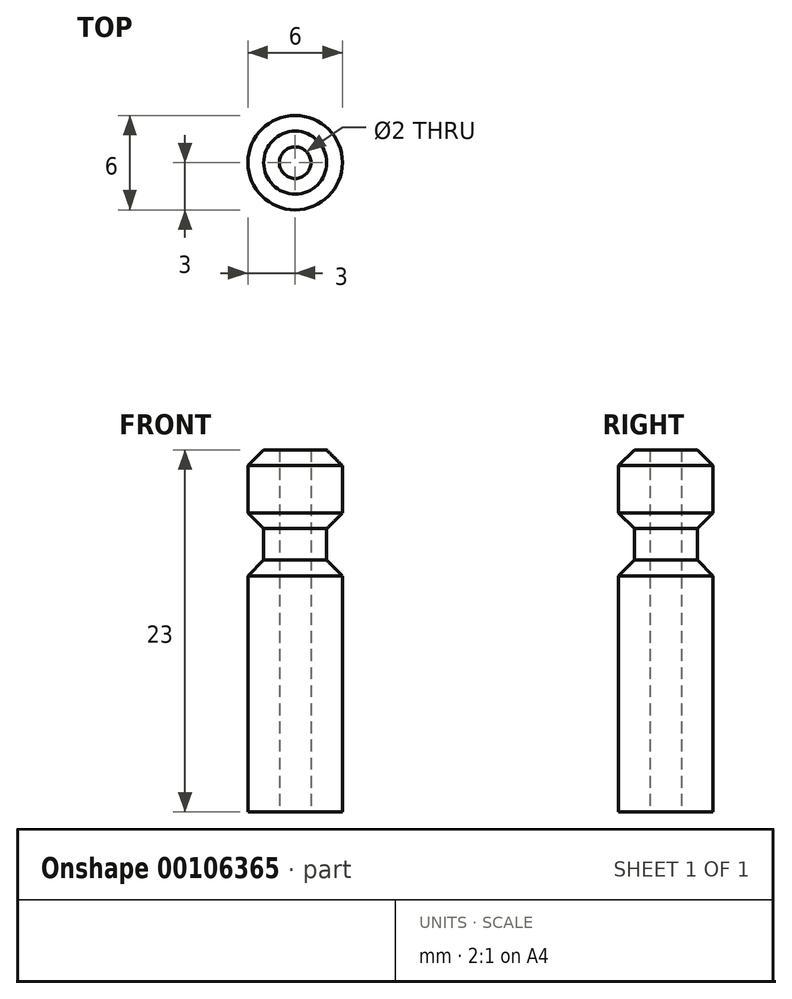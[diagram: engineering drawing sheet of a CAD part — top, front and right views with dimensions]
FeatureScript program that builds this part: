
annotation { "Feature Type Name" : "Feature", "Feature Type Description" : "" }
export const myFeature = defineFeature(function(context is Context, id is Id, definition is map)
    precondition{}
    {
        {
            var Q0;
            Q0=qCreatedBy(makeId("Top.planeOp"),FACE);
            var sketch = newSketch(context, id + "F0", { "sketchPlane" : qUnion([Q0])});
            skCircle(sketch, "E0", {"center": v(0, 0) * mm, "radius": 3 * mm});
            skSolve(sketch);
        }
        {
            var Q0;
            Q0 = qSketchRegion(id + "F0", true);
            extrude(context, id + "F1", {"entities" : qUnion([Q0]), "depth" : 16 * mm});
        }
        {
            var Q0;
            Q0=makeQuery(id+"F1.opExtrude","CAP_FACE",FACE,{"disambiguationData":[OSD([sQuery(id+"F0.wireOp",EDGE,"E0")])],"isStart":false});
            var sketch = newSketch(context, id + "F2", { "sketchPlane" : qUnion([Q0])});
            skCircle(sketch, "E1", {"center": v(0, 0) * mm, "radius": 2 * mm});
            skSolve(sketch);
        }
        {
            var Q0;
            Q0 = qSketchRegion(id + "F2", true);
            extrude(context, id + "F3", {"entities" : qUnion([Q0]), "operationType" : NewBodyOperationType.ADD, "depth" : 2 * mm});
        }
        {
            var Q0;
            Q0=makeQuery(id+"F3.opExtrude","CAP_FACE",FACE,{"disambiguationData":[OSD([sQuery(id+"F2.wireOp",EDGE,"E1")])],"isStart":false});
            var sketch = newSketch(context, id + "F4", { "sketchPlane" : qUnion([Q0])});
            skCircle(sketch, "E2", {"center": v(0, 0) * mm, "radius": 3 * mm});
            skSolve(sketch);
        }
        {
            var Q0;
            Q0 = qSketchRegion(id + "F4", true);
            extrude(context, id + "F5", {"entities" : qUnion([Q0]), "operationType" : NewBodyOperationType.ADD, "depth" : 5 * mm});
        }
        {
            var Q0;
            Q0=makeQuery(id+"F5.opExtrude","CAP_EDGE",EDGE,{"disambiguationData":[OSD([sQuery(id+"F4.wireOp",EDGE,"E2")])],"isStart":false});
            var Q1;
            Q1=makeQuery(id+"F5.opExtrude","CAP_EDGE",EDGE,{"disambiguationData":[OSD([sQuery(id+"F4.wireOp",EDGE,"E2")])],"isStart":true});
            var Q2;
            Q2=makeQuery(id+"F1.opExtrude","CAP_EDGE",EDGE,{"disambiguationData":[OSD([sQuery(id+"F0.wireOp",EDGE,"E0")])],"isStart":false});
            chamfer(context, id + "F6", {"entities" : qUnion([Q0, Q1, Q2]), "width" : 1 * mm, "tangentPropagation" : true});
        }
        {
            var Q0;
            Q0=makeQuery(id+"F1.opExtrude","CAP_FACE",FACE,{"disambiguationData":[OSD([sQuery(id+"F0.wireOp",EDGE,"E0")])],"isStart":true});
            var sketch = newSketch(context, id + "F7", { "sketchPlane" : qUnion([Q0])});
            skCircle(sketch, "E3", {"center": v(0, 0) * mm, "radius": 1 * mm});
            skSolve(sketch);
        }
        {
            var Q0;
            Q0 = qSketchRegion(id + "F7", true);
            extrude(context, id + "F8", {"entities" : qUnion([Q0]), "operationType" : NewBodyOperationType.REMOVE, "oppositeDirection" : true, "depth" : 25 * mm});
        }
    });
